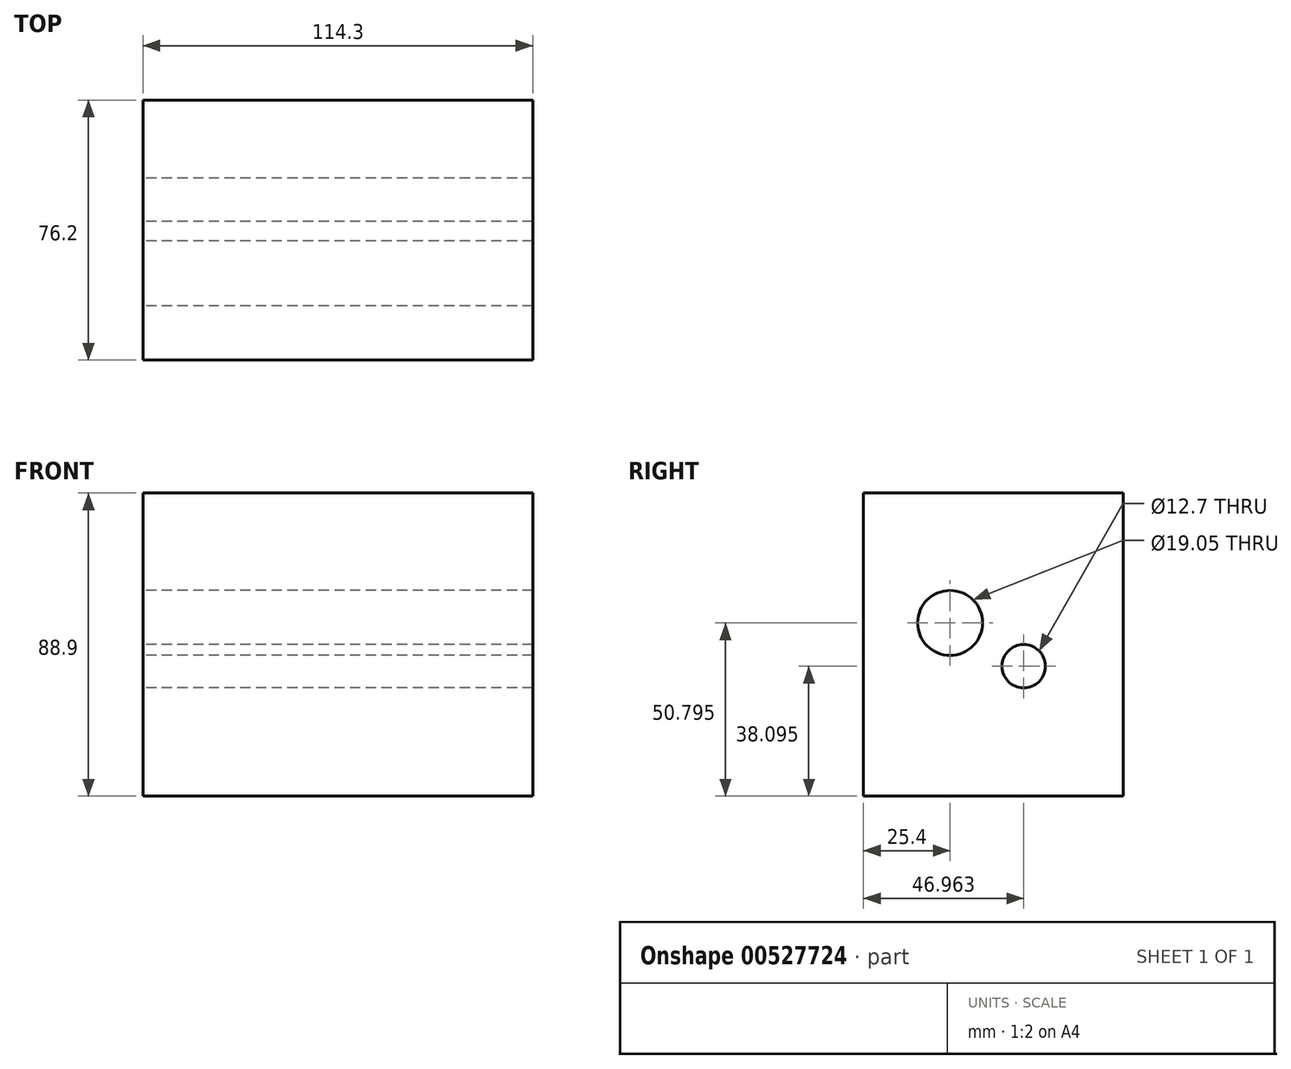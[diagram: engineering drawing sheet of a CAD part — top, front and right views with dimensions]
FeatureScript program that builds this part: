
annotation { "Feature Type Name" : "Feature", "Feature Type Description" : "" }
export const myFeature = defineFeature(function(context is Context, id is Id, definition is map)
    precondition{}
    {
        {
            var Q0;
            Q0=qCreatedBy(makeId("Front.planeOp"),FACE);
            var sketch = newSketch(context, id + "F0", { "sketchPlane" : qUnion([Q0])});
            skLineSegment(sketch, "E0.bottom", {"start": v(-47.87, 48.06) * mm, "end": v(66.43, 48.06) * mm});
            skLineSegment(sketch, "E0.top", {"start": v(-47.87, -40.84) * mm, "end": v(66.43, -40.84) * mm});
            skLineSegment(sketch, "E0.left", {"start": v(-47.87, 48.06) * mm, "end": v(-47.87, -40.84) * mm});
            skLineSegment(sketch, "E0.right", {"start": v(66.43, 48.06) * mm, "end": v(66.43, -40.84) * mm});
            skSolve(sketch);
        }
        {
            var Q0;
            Q0=makeQuery(id+"F0.imprint","IMPRINT",FACE,{"disambiguationData":[TD([[makeQuery(id+"F0.imprint","IMPRINT",EDGE,{"derivedFrom":sQuery(id+"F0.wireOp",EDGE,"E0.bottom")}),-1.0]])]});
            extrude(context, id + "F1", {"entities" : qUnion([Q0]), "depth" : 76.2 * mm, "offsetDistance" : 25.4 * mm});
        }
        {
            var Q0;
            Q0=makeQuery(id+"F1.opExtrude","SWEPT_FACE",FACE,{"disambiguationData":[OSD([sQuery(id+"F0.wireOp",EDGE,"E0.left")])]});
            var sketch = newSketch(context, id + "F2", { "sketchPlane" : qUnion([Q0])});
            skCircle(sketch, "E1", {"center": v(50.8, 9.96) * mm, "radius": 9.52 * mm});
            skCircle(sketch, "E2", {"center": v(29.24, -2.74) * mm, "radius": 6.35 * mm});
            skSolve(sketch);
        }
        {
            var Q0;
            Q0 = qSketchRegion(id + "F2", true);
            extrude(context, id + "F3", {"entities" : qUnion([Q0]), "operationType" : NewBodyOperationType.REMOVE, "endBound" : BoundingType.UP_TO_NEXT, "oppositeDirection" : true, "depth" : 25.4 * mm, "offsetDistance" : 25.4 * mm});
        }
    });
